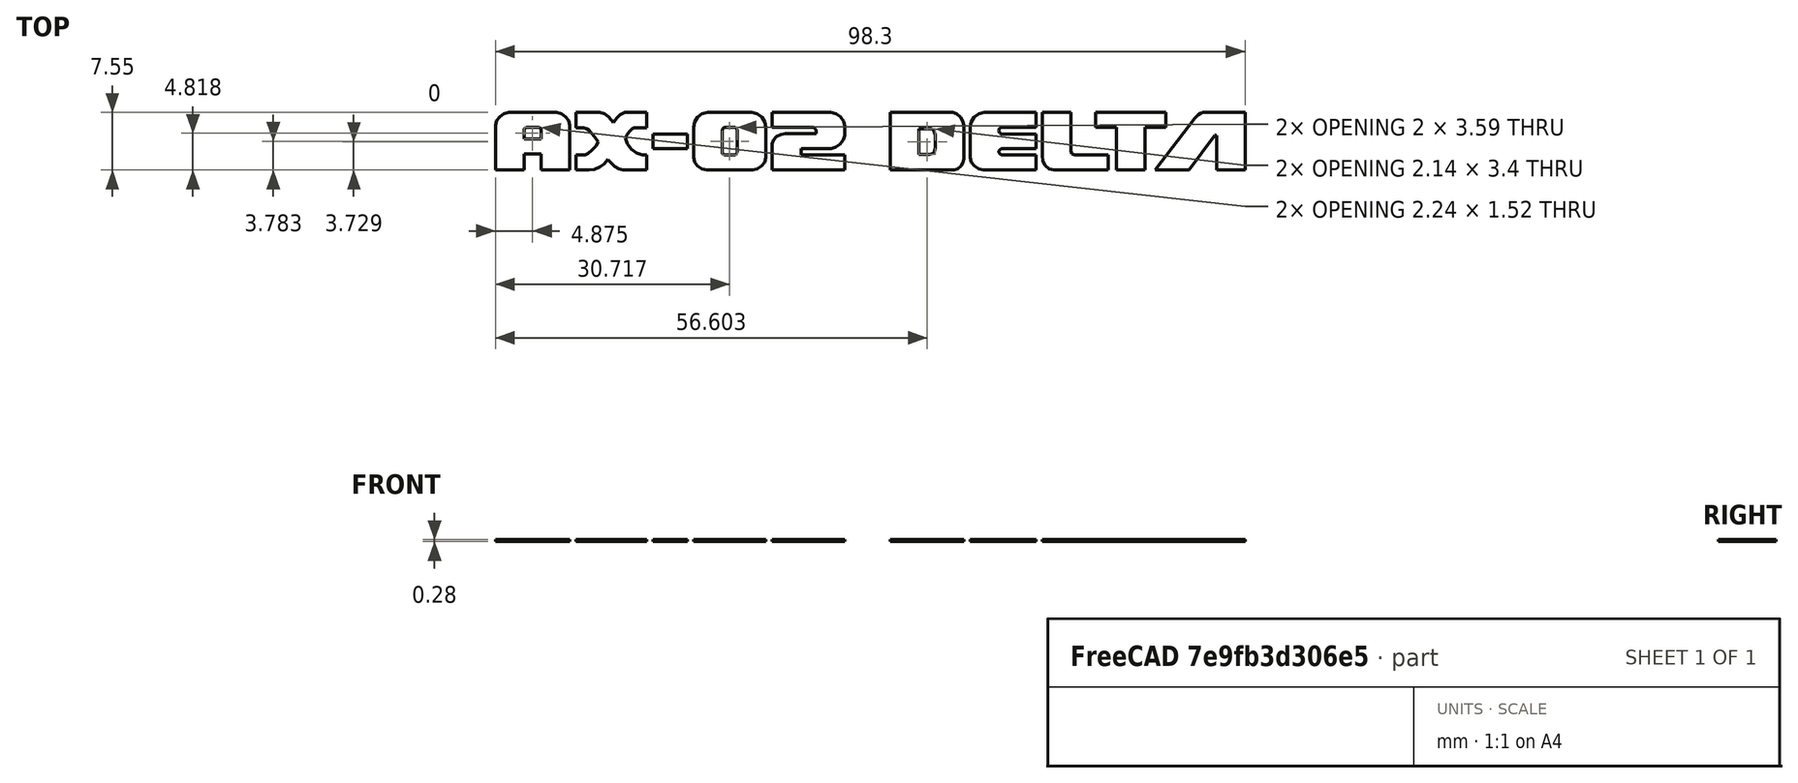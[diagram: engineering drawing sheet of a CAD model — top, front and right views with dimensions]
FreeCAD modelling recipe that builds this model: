
FCSTD DOCUMENT  (FreeCAD 0.16R6707 (Git))
Label: AX-02_Logo_3D
License: CreativeCommons Attribution-NonCommercial
LicenseURL: http://creativecommons.org/licenses/by-nc/4.0/
objects: Part::Feature×14, Part::Extrusion×10, Part::Cut×3, Part::Compound×1
note: 28 computed .brp shape members not serialized (recipe doc carries the construction recipe); baked Part::Feature solids carry a one-line shape summary decoded from their .brp

FEATURE [Part::Feature] Face
  shape: bbox 2.245 x 1.519 x 2e-07 mm, 1 faces, 0 solids (baked)
FEATURE [Part::Feature] Face001
  shape: bbox 9.758 x 7.54 x 2e-07 mm, 1 faces, 0 solids (baked)
FEATURE [Part::Feature] Face002
  shape: bbox 9.288 x 7.54 x 2e-07 mm, 1 faces, 0 solids (baked)
FEATURE [Part::Feature] Face003
  shape: bbox 4.503 x 1.922 x 2e-07 mm, 1 faces, 0 solids (baked)
FEATURE [Part::Feature] Face004
  shape: bbox 2.003 x 3.589 x 2e-07 mm, 1 faces, 0 solids (baked)
FEATURE [Part::Feature] Face005
  shape: bbox 9.503 x 7.54 x 2e-07 mm, 1 faces, 0 solids (baked)
FEATURE [Part::Feature] Face006
  shape: bbox 9.516 x 7.54 x 2e-07 mm, 1 faces, 0 solids (baked)
FEATURE [Part::Feature] Face007
  shape: bbox 2.137 x 3.401 x 2e-07 mm, 1 faces, 0 solids (baked)
FEATURE [Part::Feature] Face009
  shape: bbox 8.642 x 7.54 x 2e-07 mm, 1 faces, 0 solids (baked)
FEATURE [Part::Feature] Face010
  shape: bbox 8.642 x 7.54 x 2e-07 mm, 1 faces, 0 solids (baked)
FEATURE [Part::Feature] Face011
  shape: bbox 9.261 x 7.54 x 2e-07 mm, 1 faces, 0 solids (baked)
FEATURE [Part::Feature] Face012
  shape: bbox 11.79 x 7.554 x 2e-07 mm, 1 faces, 0 solids (baked)
FEATURE [Part::Cut] Cut
  Base = -> Face005
  Tool = -> Face004
FEATURE [Part::Cut] Cut001
  Base = -> Face001
  Tool = -> Face
FEATURE [Part::Feature] Face013
  shape: bbox 9.664 x 7.54 x 2e-07 mm, 1 faces, 0 solids (baked)
FEATURE [Part::Cut] Cut002
  Base = -> Face013
  Tool = -> Face007
FEATURE [Part::Extrusion] Extrude_Face002  label="Face002_Extrude"
  Base = -> Face002
  Dir = (0,0,0.28)
  Solid = false
FEATURE [Part::Extrusion] Extrude_Face003  label="Face003_Extrude"
  Base = -> Face003
  Dir = (0,0,0.28)
  Solid = false
FEATURE [Part::Extrusion] Extrude_Face006  label="Face006_Extrude"
  Base = -> Face006
  Dir = (0,0,0.28)
  Solid = false
FEATURE [Part::Extrusion] Extrude_Face009  label="Face009_Extrude"
  Base = -> Face009
  Dir = (0,0,0.28)
  Solid = false
FEATURE [Part::Extrusion] Extrude_Face010  label="Face010_Extrude"
  Base = -> Face010
  Dir = (0,0,0.28)
  Solid = false
FEATURE [Part::Extrusion] Extrude_Face011  label="Face011_Extrude"
  Base = -> Face011
  Dir = (0,0,0.28)
  Solid = false
FEATURE [Part::Extrusion] Extrude_Face012  label="Face012_Extrude"
  Base = -> Face012
  Dir = (0,0,0.28)
  Solid = false
FEATURE [Part::Extrusion] Extrude_Cut  label="Cut_Extrude"
  Base = -> Cut
  Dir = (0,0,0.28)
  Solid = false
FEATURE [Part::Extrusion] Extrude_Cut001  label="Cut001_Extrude"
  Base = -> Cut001
  Dir = (0,0,0.28)
  Solid = false
FEATURE [Part::Extrusion] Extrude_Cut002  label="Cut002_Extrude"
  Base = -> Cut002
  Dir = (0,0,0.28)
  Solid = false
FEATURE [Part::Compound] Compound
  Links = -> [Extrude_Cut,Extrude_Face012,Extrude_Cut002,Extrude_Face010,Extrude_Cut001,Extrude_Face003,Extrude_Face002,Extrude_Face006,Extrude_Face009,Extrude_Face011]
FEATURE [Part::Feature] Compound001  label="Logo"
  shape: bbox 98.3 x 7.554 x 0.28 mm, 242 faces, 10 solids (baked)
